# Revit family: Sink-Undermount-Kitchen-KALLISTA-Bacifiore-L20515
name_source: partatom
category: Plumbing Fixtures
units: mm (PartAtom-declared; Revit-internal decimal feet)

## family parameters
Cut with Voids When Loaded = No
Host = Face
Maintain Annotation Orientation = No
OmniClass Number = 23.31.13.00
OmniClass Title = Sinks
Part Type = Normal
Room Calculation Point = No
Round Connector Dimension = Use Diameter
Shared = No

## types (1)
- PDS-Polished Distressed Steel
    ADA Compliant = No
    Assembly Code = D2010400
    CW Connection = No
    Cold Water Inlet = Cold Water Inlet
    Date Modified = 05/05/2025
    Default Elevation = 36"
    Description = 30 inch Apron Butler Front Sink
    Drain Included = No
    Finish = Kallista-Metal-PDS-Polished_Distressed_Steel
    HW Connection = No
    Height = 7"
    Hot Water Inlet = Hot Water Inlet
    Length = 28"
    Manufacturer = Kallista Co.
    Master Format 2014 = 22 41 16
    Master Format 2014 Name = Residential Lavatories and Sinks
    Material = Premium Metal Construction
    Model = L20515-00-PDS
    Product Documentation Link = https://techcomm.kohler.com
    Product Name = Bacifiore
    Product Page URL = https://www.kallista.com
    Type = 1
    URL = https://www.kallista.com
    Vent Connection = No
    Waste Connection = Yes
    Waste Water Outlet = Waste Water Outlet
    WaterSense Certified = No
    Width = 21 3/16"

## geometry (parser evidence)
native form markers: Sweep x4
no freeform markers — native parametric forms only
